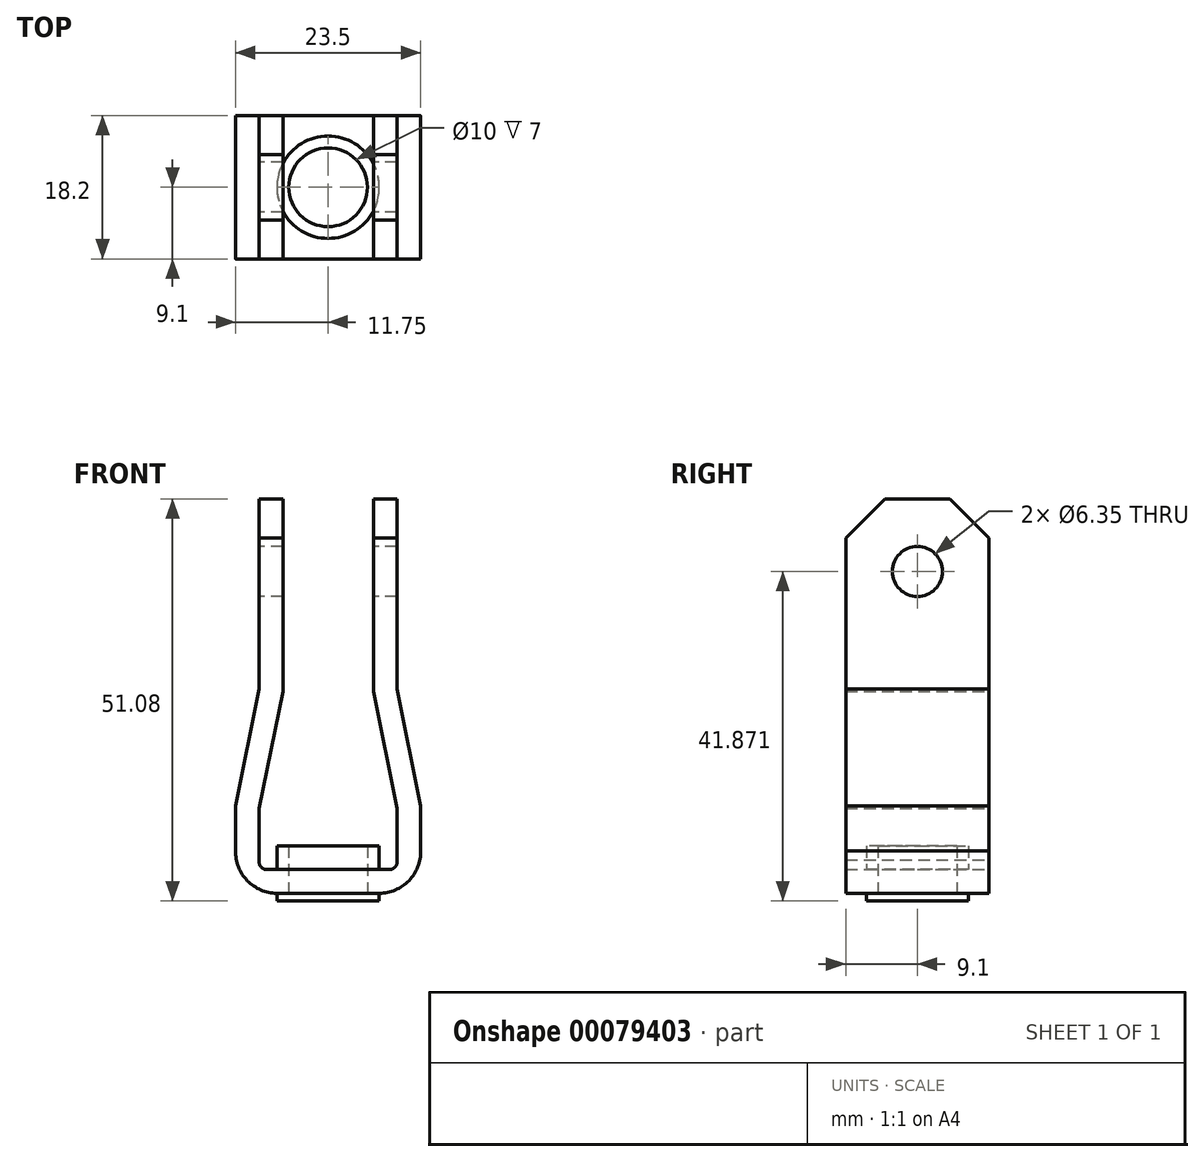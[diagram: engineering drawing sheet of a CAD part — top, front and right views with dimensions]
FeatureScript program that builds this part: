
annotation { "Feature Type Name" : "Feature", "Feature Type Description" : "" }
export const myFeature = defineFeature(function(context is Context, id is Id, definition is map)
    precondition{}
    {
        {
            var Q0;
            Q0=qCreatedBy(makeId("Front.planeOp"),FACE);
            var sketch = newSketch(context, id + "F0", { "sketchPlane" : qUnion([Q0])});
            skLineSegment(sketch, "E0", {"start": v(0, 45.88) * mm, "end": v(0, -39.97) * mm});
            skLineSegment(sketch, "E1", {"start": v(0, 0) * mm, "end": v(-6.5, 0) * mm});
            skArc(sketch, "E2", {"start": v(-6.5, 0) * mm, "mid": v(-10.27, 1.59) * mm, "end": v(-11.75, 5.4) * mm});
            skLineSegment(sketch, "E3", {"start": v(-11.75, 5.4) * mm, "end": v(-11.75, 11.1) * mm});
            skLineSegment(sketch, "E4", {"start": v(-11.75, 11.1) * mm, "end": v(-8.75, 25.92) * mm});
            skLineSegment(sketch, "E5", {"start": v(-8.75, 25.92) * mm, "end": v(-8.75, 45.12) * mm});
            skLineSegment(sketch, "E6.0", {"start": v(-8.75, 4.2) * mm, "end": v(-8.75, 10.8) * mm});
            skLineSegment(sketch, "E7.0", {"start": v(-8.75, 10.8) * mm, "end": v(-5.75, 25.62) * mm});
            skLineSegment(sketch, "E8.0", {"start": v(-5.75, 25.62) * mm, "end": v(-5.75, 45.12) * mm});
            skLineSegment(sketch, "E9", {"start": v(-8.75, 45.12) * mm, "end": v(-5.75, 45.12) * mm});
            skLineSegment(sketch, "E10.MirrorCS", {"start": v(11.75, 11.1) * mm, "end": v(8.75, 25.92) * mm});
            skLineSegment(sketch, "E11.MirrorCS", {"start": v(8.75, 45.12) * mm, "end": v(5.75, 45.12) * mm});
            skLineSegment(sketch, "E12.MirrorCS", {"start": v(11.75, 5.4) * mm, "end": v(11.75, 11.1) * mm});
            skLineSegment(sketch, "E13.MirrorCS", {"start": v(8.75, 25.92) * mm, "end": v(8.75, 45.12) * mm});
            skLineSegment(sketch, "E14.MirrorCS", {"start": v(8.75, 4.2) * mm, "end": v(8.75, 10.8) * mm});
            skLineSegment(sketch, "E15.MirrorCS", {"start": v(5.75, 25.62) * mm, "end": v(5.75, 45.12) * mm});
            skLineSegment(sketch, "E16.MirrorCS", {"start": v(8.75, 10.8) * mm, "end": v(5.75, 25.62) * mm});
            skLineSegment(sketch, "E17.MirrorCS", {"start": v(0, 0) * mm, "end": v(6.5, 0) * mm});
            skArc(sketch, "E18.MirrorCS", {"start": v(6.5, 0) * mm, "mid": v(10.27, 1.59) * mm, "end": v(11.75, 5.4) * mm});
            skLineSegment(sketch, "E19.0", {"start": v(0, 3) * mm, "end": v(-7.77, 3) * mm});
            skArc(sketch, "E20", {"start": v(-8.75, 4.2) * mm, "mid": v(-8.55, 3.37) * mm, "end": v(-7.77, 3) * mm});
            skLineSegment(sketch, "E21.0", {"start": v(0, 3) * mm, "end": v(7.77, 3) * mm});
            skArc(sketch, "E22", {"start": v(7.77, 3) * mm, "mid": v(8.55, 3.37) * mm, "end": v(8.75, 4.2) * mm});
            skSolve(sketch);
        }
        {
            var Q0;
            {var subQ0=sQuery(id+"F0.wireOp",EDGE,"E1");Q0=makeQuery(id+"F0.imprint","IMPRINT",FACE,{"disambiguationData":[TD([[makeQuery(id+"F0.imprint","IMPRINT",EDGE,{"derivedFrom":subQ0}),-1.0]])]});}
            var Q1;
            Q1=makeQuery(id+"F0.imprint","IMPRINT",FACE,{"disambiguationData":[TD([[makeQuery(id+"F0.imprint","IMPRINT",EDGE,{"derivedFrom":sQuery(id+"F0.wireOp",EDGE,"E10.MirrorCS")}),1.0]])]});
            extrude(context, id + "F1", {"entities" : qUnion([Q0, Q1]), "endBound" : BoundingType.SYMMETRIC, "depth" : 18.2 * mm});
        }
        {
            var Q0;
            Q0=makeQuery(id+"F1.opExtrude","SWEPT_FACE",FACE,{"disambiguationData":[OSD([sQuery(id+"F0.wireOp",EDGE,"E5")])]});
            var sketch = newSketch(context, id + "F2", { "sketchPlane" : qUnion([Q0])});
            skLineSegment(sketch, "E23", {"start": v(-9.1, 45.12) * mm, "end": v(-4.15, 50.07) * mm});
            skLineSegment(sketch, "E24", {"start": v(9.1, 45.12) * mm, "end": v(4.15, 50.07) * mm});
            skLineSegment(sketch, "E25", {"start": v(-4.15, 50.07) * mm, "end": v(4.15, 50.07) * mm});
            skLineSegment(sketch, "E26", {"start": v(-9.1, 45.12) * mm, "end": v(9.1, 45.12) * mm});
            skSolve(sketch);
        }
        {
            var Q0;
            Q0=makeQuery(id+"F2.imprint","IMPRINT",FACE,{"disambiguationData":[TD([[makeQuery(id+"F2.imprint","IMPRINT",EDGE,{"derivedFrom":sQuery(id+"F2.wireOp",EDGE,"E23")}),-1.0]])]});
            extrude(context, id + "F3", {"entities" : qUnion([Q0]), "operationType" : NewBodyOperationType.ADD, "oppositeDirection" : true, "depth" : 3 * mm});
        }
        {
            var Q0;
            Q0=makeQuery(id+"F1.opExtrude","SWEPT_FACE",FACE,{"disambiguationData":[OSD([sQuery(id+"F0.wireOp",EDGE,"E13.MirrorCS")])]});
            var sketch = newSketch(context, id + "F4", { "sketchPlane" : qUnion([Q0])});
            skLineSegment(sketch, "E27", {"start": v(-9.1, 45.12) * mm, "end": v(9.1, 45.12) * mm});
            skLineSegment(sketch, "E28", {"start": v(-9.1, 45.12) * mm, "end": v(-9.1, 54.13) * mm});
            skLineSegment(sketch, "E29", {"start": v(9.04, 45.2) * mm, "end": v(9.06, 54.24) * mm});
            skLineSegment(sketch, "E30", {"start": v(9.1, 45.12) * mm, "end": v(4.16, 50.08) * mm});
            skLineSegment(sketch, "E31", {"start": v(-4.15, 50.07) * mm, "end": v(4.16, 50.08) * mm});
            skLineSegment(sketch, "E32", {"start": v(-9.1, 45.12) * mm, "end": v(-4.15, 50.07) * mm});
            skSolve(sketch);
        }
        {
            var Q0;
            Q0=makeQuery(id+"F4.imprint","IMPRINT",FACE,{"disambiguationData":[TD([[makeQuery(id+"F4.imprint","IMPRINT",EDGE,{"derivedFrom":sQuery(id+"F4.wireOp",EDGE,"E30")}),1.0]])]});
            extrude(context, id + "F5", {"entities" : qUnion([Q0]), "operationType" : NewBodyOperationType.ADD, "oppositeDirection" : true, "depth" : 3 * mm});
        }
        {
            var Q0;
            Q0=makeQuery(id+"F3.boolean.opBoolean","MERGE",FACE,{"derivedFrom":[makeQuery(id+"F1.opExtrude","SWEPT_FACE",FACE,{"disambiguationData":[OSD([sQuery(id+"F0.wireOp",EDGE,"E5")])]}),makeQuery(id+"F3.opExtrude","CAP_FACE",FACE,{"disambiguationData":[OSD([sQuery(id+"F2.wireOp",EDGE,"E23"),sQuery(id+"F2.wireOp",EDGE,"E24"),sQuery(id+"F2.wireOp",EDGE,"E25"),sQuery(id+"F2.wireOp",EDGE,"E26")])],"isStart":true})]});
            var sketch = newSketch(context, id + "F6", { "sketchPlane" : qUnion([Q0])});
            skLineSegment(sketch, "E33", {"start": v(0, 50.07) * mm, "end": v(0, 40.87) * mm});
            skCircle(sketch, "E34", {"center": v(0, 40.87) * mm, "radius": 4.2 * mm});
            skSolve(sketch);
        }
        {
            var Q0;
            Q0=sQuery(id+"F6.wireOp",VERTEX,"E33.end");
            var Q1;
            Q1=makeQuery(id+"F1.opExtrude","SWEPT_BODY",BODY,{"disambiguationData":[OSD([sQuery(id+"F0.wireOp",EDGE,"E1"),sQuery(id+"F0.wireOp",EDGE,"E2"),sQuery(id+"F0.wireOp",EDGE,"E3"),sQuery(id+"F0.wireOp",EDGE,"E4"),sQuery(id+"F0.wireOp",EDGE,"E5"),sQuery(id+"F0.wireOp",EDGE,"E6.0"),sQuery(id+"F0.wireOp",EDGE,"E7.0"),sQuery(id+"F0.wireOp",EDGE,"E8.0"),sQuery(id+"F0.wireOp",EDGE,"E9"),sQuery(id+"F0.wireOp",EDGE,"E10.MirrorCS"),sQuery(id+"F0.wireOp",EDGE,"E11.MirrorCS"),sQuery(id+"F0.wireOp",EDGE,"E12.MirrorCS"),sQuery(id+"F0.wireOp",EDGE,"E13.MirrorCS"),sQuery(id+"F0.wireOp",EDGE,"E14.MirrorCS"),sQuery(id+"F0.wireOp",EDGE,"E15.MirrorCS"),sQuery(id+"F0.wireOp",EDGE,"E16.MirrorCS"),sQuery(id+"F0.wireOp",EDGE,"E17.MirrorCS"),sQuery(id+"F0.wireOp",EDGE,"E18.MirrorCS"),sQuery(id+"F0.wireOp",EDGE,"E19.0"),sQuery(id+"F0.wireOp",EDGE,"E20"),sQuery(id+"F0.wireOp",EDGE,"E21.0"),sQuery(id+"F0.wireOp",EDGE,"E22")])]});
            hole(context, id + "F7", {"style" : HoleStyle.SIMPLE, "endStyle" : HoleEndStyle.THROUGH, "holeDiameter" : 6.35 * mm, "locations" : qUnion([Q0]), "scope" : qUnion([Q1]), "isTappedThrough" : true});
        }
        {
            var Q0;
            Q0=makeQuery(id+"F1.opExtrude","SWEPT_FACE",FACE,{"disambiguationData":[OSD([sQuery(id+"F0.wireOp",EDGE,"E1"),sQuery(id+"F0.wireOp",EDGE,"E17.MirrorCS")])]});
            var sketch = newSketch(context, id + "F8", { "sketchPlane" : qUnion([Q0])});
            skCircle(sketch, "E35", {"center": v(0, 0) * mm, "radius": 5 * mm});
            skSolve(sketch);
        }
        {
            var Q0;
            Q0=sQuery(id+"F8.wireOp",VERTEX,"E35.center");
            var Q1;
            Q1=makeQuery(id+"F1.opExtrude","SWEPT_BODY",BODY,{"disambiguationData":[OSD([sQuery(id+"F0.wireOp",EDGE,"E1"),sQuery(id+"F0.wireOp",EDGE,"E2"),sQuery(id+"F0.wireOp",EDGE,"E3"),sQuery(id+"F0.wireOp",EDGE,"E4"),sQuery(id+"F0.wireOp",EDGE,"E5"),sQuery(id+"F0.wireOp",EDGE,"E6.0"),sQuery(id+"F0.wireOp",EDGE,"E7.0"),sQuery(id+"F0.wireOp",EDGE,"E8.0"),sQuery(id+"F0.wireOp",EDGE,"E9"),sQuery(id+"F0.wireOp",EDGE,"E10.MirrorCS"),sQuery(id+"F0.wireOp",EDGE,"E11.MirrorCS"),sQuery(id+"F0.wireOp",EDGE,"E12.MirrorCS"),sQuery(id+"F0.wireOp",EDGE,"E13.MirrorCS"),sQuery(id+"F0.wireOp",EDGE,"E14.MirrorCS"),sQuery(id+"F0.wireOp",EDGE,"E15.MirrorCS"),sQuery(id+"F0.wireOp",EDGE,"E16.MirrorCS"),sQuery(id+"F0.wireOp",EDGE,"E17.MirrorCS"),sQuery(id+"F0.wireOp",EDGE,"E18.MirrorCS"),sQuery(id+"F0.wireOp",EDGE,"E19.0"),sQuery(id+"F0.wireOp",EDGE,"E20"),sQuery(id+"F0.wireOp",EDGE,"E21.0"),sQuery(id+"F0.wireOp",EDGE,"E22")])]});
            hole(context, id + "F9", {"style" : HoleStyle.SIMPLE, "endStyle" : HoleEndStyle.THROUGH, "holeDiameter" : 10 * mm, "locations" : qUnion([Q0]), "scope" : qUnion([Q1]), "isTappedThrough" : true});
        }
        {
            var Q0;
            Q0=makeQuery(id+"F1.opExtrude","SWEPT_FACE",FACE,{"disambiguationData":[OSD([sQuery(id+"F0.wireOp",EDGE,"E1"),sQuery(id+"F0.wireOp",EDGE,"E17.MirrorCS")])]});
            var sketch = newSketch(context, id + "F10", { "sketchPlane" : qUnion([Q0])});
            skCircle(sketch, "E36", {"center": v(0, 0) * mm, "radius": 6.5 * mm});
            skCircle(sketch, "E37", {"center": v(0, 0) * mm, "radius": 5 * mm});
            skSolve(sketch);
        }
        {
            var Q0;
            Q0=makeQuery(id+"F10.imprint","IMPRINT",FACE,{"disambiguationData":[TD([[makeQuery(id+"F10.imprint","IMPRINT",EDGE,{"derivedFrom":sQuery(id+"F10.wireOp",EDGE,"E37")}),-1.0]])]});
            extrude(context, id + "F11", {"entities" : qUnion([Q0]), "operationType" : NewBodyOperationType.ADD, "depth" : 1 * mm});
        }
        {
            var Q0;
            Q0=makeQuery(id+"F1.opExtrude","SWEPT_FACE",FACE,{"disambiguationData":[OSD([sQuery(id+"F0.wireOp",EDGE,"E19.0"),sQuery(id+"F0.wireOp",EDGE,"E21.0")])]});
            var sketch = newSketch(context, id + "F12", { "sketchPlane" : qUnion([Q0])});
            skCircle(sketch, "E38", {"center": v(0, 0) * mm, "radius": 6.5 * mm});
            skCircle(sketch, "E39", {"center": v(0, 0) * mm, "radius": 5 * mm});
            skSolve(sketch);
        }
        {
            var Q0;
            Q0=makeQuery(id+"F12.imprint","IMPRINT",FACE,{"disambiguationData":[TD([[makeQuery(id+"F12.imprint","IMPRINT",EDGE,{"derivedFrom":sQuery(id+"F12.wireOp",EDGE,"E38")}),1.0]])]});
            extrude(context, id + "F13", {"entities" : qUnion([Q0]), "operationType" : NewBodyOperationType.ADD, "depth" : 3 * mm});
        }
    });
